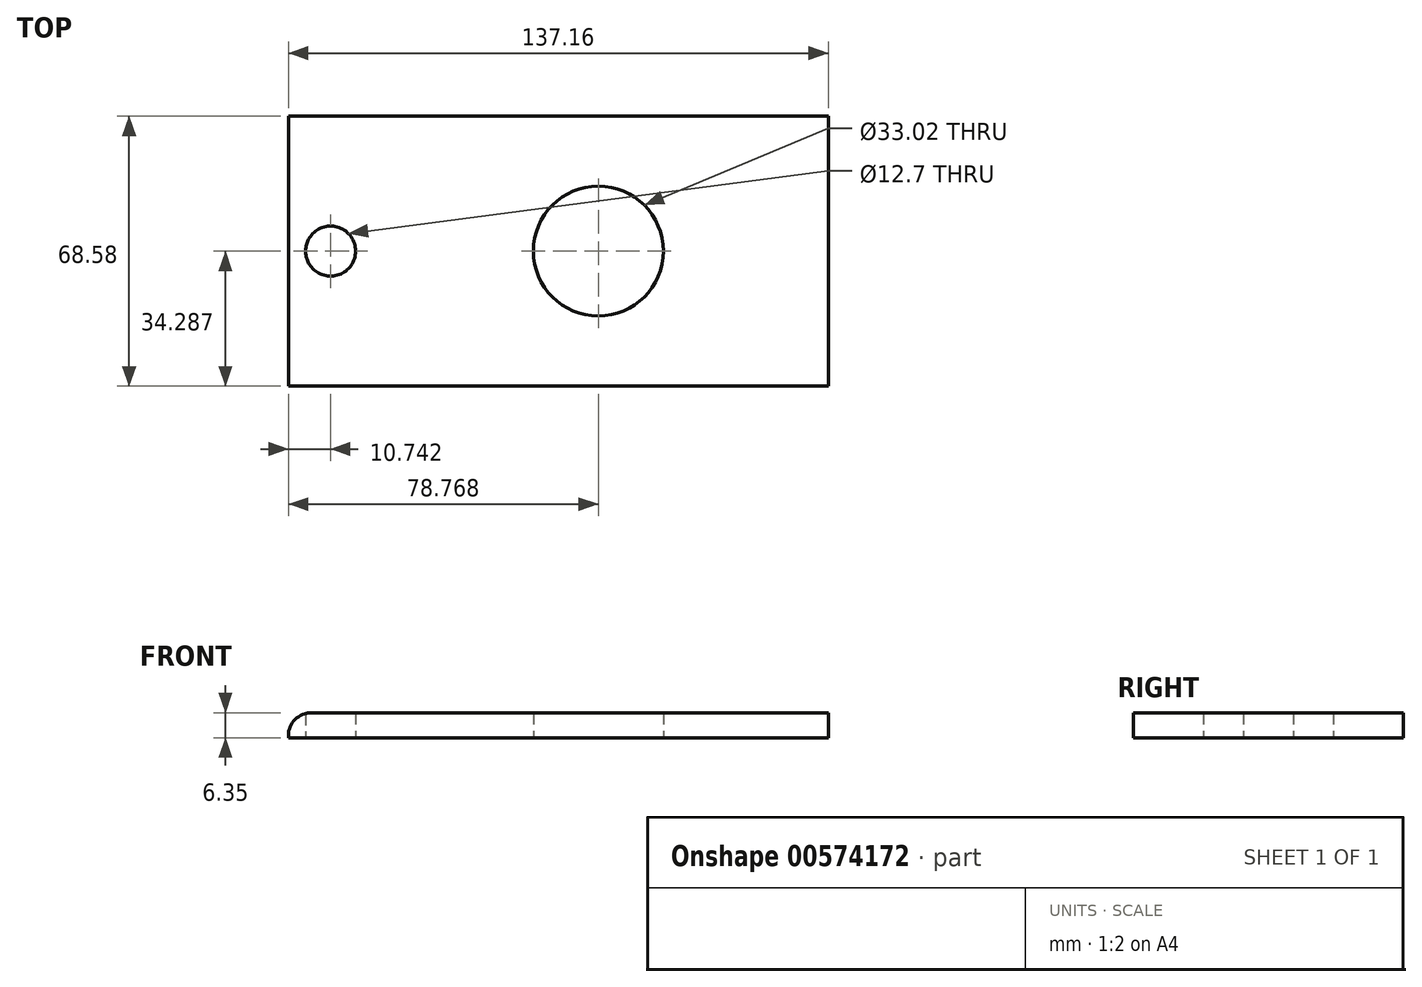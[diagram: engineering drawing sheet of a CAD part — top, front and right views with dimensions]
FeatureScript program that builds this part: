
annotation { "Feature Type Name" : "Feature", "Feature Type Description" : "" }
export const myFeature = defineFeature(function(context is Context, id is Id, definition is map)
    precondition{}
    {
        {
            var Q0;
            Q0=qCreatedBy(makeId("Top.planeOp"),FACE);
            var sketch = newSketch(context, id + "F0", { "sketchPlane" : qUnion([Q0])});
            skLineSegment(sketch, "E0.bottom", {"start": v(-77.59, -15.02) * mm, "end": v(59.57, -15.02) * mm});
            skLineSegment(sketch, "E0.top", {"start": v(-77.59, 53.56) * mm, "end": v(59.57, 53.56) * mm});
            skLineSegment(sketch, "E0.left", {"start": v(-77.59, -15.02) * mm, "end": v(-77.59, 53.56) * mm});
            skLineSegment(sketch, "E0.right", {"start": v(59.57, -15.02) * mm, "end": v(59.57, 53.56) * mm});
            skLineSegment(sketch, "E1", {"start": v(-77.59, 19.27) * mm, "end": v(59.57, 19.27) * mm});
            skCircle(sketch, "E2", {"center": v(-66.85, 19.27) * mm, "radius": 6.35 * mm});
            skCircle(sketch, "E3", {"center": v(1.18, 19.27) * mm, "radius": 16.51 * mm});
            skSolve(sketch);
        }
        {
            var Q0;
            Q0 = qSketchRegion(id + "F0", true);
            extrude(context, id + "F1", {"entities" : qUnion([Q0]), "depth" : 6.35 * mm, "offsetDistance" : 25.4 * mm});
        }
        {
            var Q0;
            Q0=makeQuery(id+"F1.opExtrude","CAP_EDGE",EDGE,{"disambiguationData":[OSD([sQuery(id+"F0.wireOp",EDGE,"E0.left")])],"isStart":false});
            fillet(context, id + "F2", {"entities" : qUnion([Q0]), "radius" : 5.84 * mm, "tangentPropagation" : true, "allowEdgeOverflow" : false});
        }
    });
